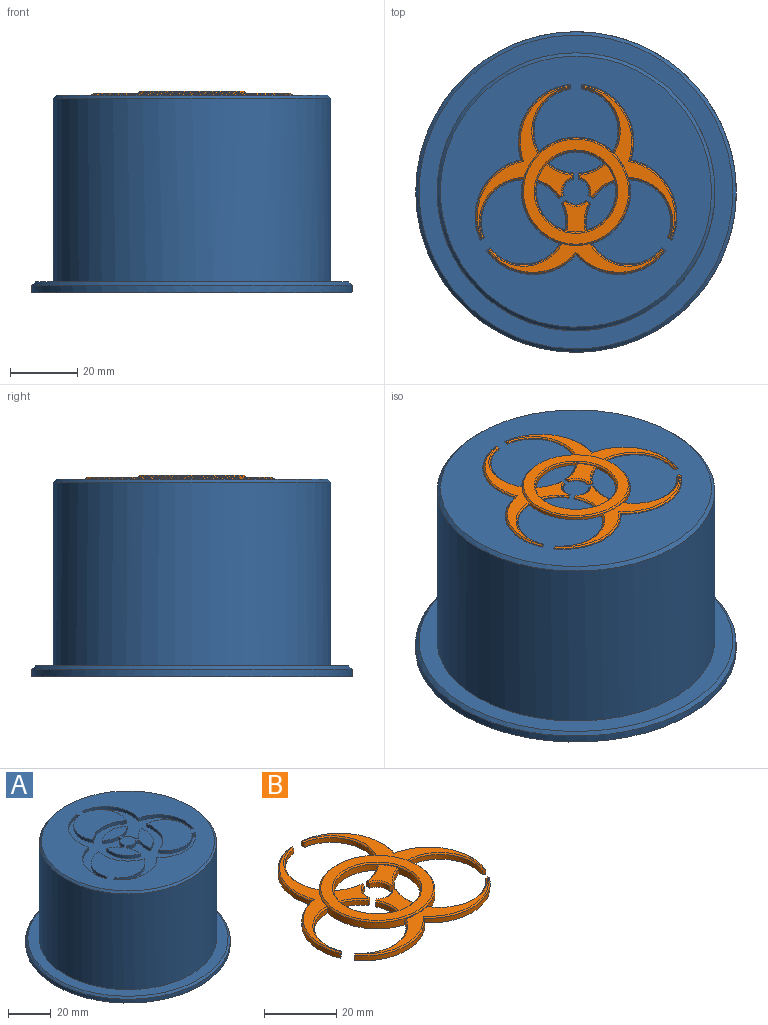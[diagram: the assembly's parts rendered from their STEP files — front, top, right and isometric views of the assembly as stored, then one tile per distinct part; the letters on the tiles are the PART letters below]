
ASSEMBLY  parts=2 mates=1
PART A: 85 faces, bbox 95.3x95.3x58.8 mm
  f0: plane 80.55x80.55mm, normal (0,0,1), area 3682.3mm2, adj f43,f46,f47,f48,f49,f53,f54,f55
  f1: plane 38.88x4.14mm, normal (0,0.71,-0.71), area 206.1mm2, adj f4,f12,f15,f35
  f2: plane 9.69x1.97mm, normal (0,1,-0.09), area 9.4mm2, adj f4,f15,f31
  f3: plane 38.88x4.14mm, normal (0,-0.71,-0.71), area 206.1mm2, adj f14,f15,f21,f39
  f4: cylinder r=50mm len=31.49mm, axis (1,0,0), area 469.7mm2, adj f1,f2,f15,f30
  f5: cylinder r=50mm len=34.5mm, axis (-0.5,-0.87,0), area 469.7mm2, adj f6,f7,f15,f41
  f6: plane 35.55x19.44mm, normal (0.61,-0.35,-0.71), area 206.1mm2, adj f5,f15,f24,f37
  f7: plane 9.69x1.72mm, normal (0.86,-0.5,-0.09), area 9.4mm2, adj f5,f15,f36
  f8: plane 35.55x19.44mm, normal (-0.61,0.35,-0.71), area 206.1mm2, adj f15,f27,f29,f34
  f9: plane 9.69x1.72mm, normal (-0.86,0.5,-0.09), area 9.4mm2, adj f15,f29,f33
  f10: plane 9.69x1.97mm, normal (0,-1,-0.09), area 9.4mm2, adj f15,f22,f25
  f11: plane 9.69x1.97mm, normal (0,1,-0.09), area 9.4mm2, adj f13,f15,f26
  f12: plane 38.88x4.14mm, normal (0,-0.71,-0.71), area 206.1mm2, adj f1,f15,f22,f24
  f13: cylinder r=50mm len=31.49mm, axis (1,0,0), area 469.7mm2, adj f11,f15,f21,f28
  f14: cylinder r=50mm len=31.49mm, axis (1,0,0), area 469.7mm2, adj f3,f15,f20,f40
  f15: cylinder r=38.88mm len=77.75mm, axis (0,0,-1), area 10153.5mm2, adj f1,f2,f3,f4,f5,f6,f7,f8
  f16: plane 95.25x95.25mm, normal (0,0,-1), area 2377.8mm2, adj f15,f17
  f17: cylinder r=47.62mm len=95.25mm, axis (0,0,-1), area 650.8mm2, adj f16,f42
  f18: plane 93.25x93.25mm, normal (0,0,1), area 1477.4mm2, adj f19,f42
  f19: cylinder r=41.27mm len=82.55mm, axis (0,0,-1), area 14146.9mm2, adj f18,f43
  f20: plane 9.69x1.97mm, normal (0,-1,-0.09), area 9.4mm2, adj f14,f15,f38
  f21: plane 38.88x4.14mm, normal (0,0.71,-0.71), area 206.1mm2, adj f3,f13,f15,f27
  f22: cylinder r=50mm len=31.49mm, axis (1,0,0), area 469.7mm2, adj f10,f12,f15,f23
  f23: cylinder r=50mm len=34.5mm, axis (-0.5,-0.87,0), area 469.7mm2, adj f15,f22,f24,f25
  f24: plane 33.67x22.92mm, normal (-0.61,0.35,-0.71), area 206.1mm2, adj f6,f12,f15,f23
  f25: plane 9.69x1.71mm, normal (-0.86,0.5,-0.09), area 9.4mm2, adj f10,f15,f23
  f26: plane 9.69x1.71mm, normal (0.86,-0.5,-0.09), area 9.4mm2, adj f11,f15,f28
  f27: plane 33.67x22.92mm, normal (0.61,-0.35,-0.71), area 206.1mm2, adj f8,f15,f21,f28
  f28: cylinder r=50mm len=34.5mm, axis (-0.5,-0.87,0), area 469.7mm2, adj f13,f15,f26,f27
  f29: cylinder r=50mm len=34.5mm, axis (-0.5,-0.87,0), area 469.7mm2, adj f8,f9,f15,f32
  f30: cylinder r=50mm len=34.5mm, axis (-0.5,0.87,0), area 469.7mm2, adj f4,f15,f31,f35
  f31: plane 9.69x1.71mm, normal (-0.86,-0.5,-0.09), area 9.4mm2, adj f2,f15,f30
  f32: cylinder r=50mm len=34.5mm, axis (-0.5,0.87,0), area 469.7mm2, adj f15,f29,f33,f34
  f33: plane 9.69x1.72mm, normal (0.86,0.5,-0.09), area 9.4mm2, adj f9,f15,f32
  f34: plane 35.55x19.44mm, normal (0.61,0.35,-0.71), area 206.1mm2, adj f8,f15,f32,f35
  f35: plane 33.67x22.92mm, normal (-0.61,-0.35,-0.71), area 206.1mm2, adj f1,f15,f30,f34
  f36: plane 9.69x1.72mm, normal (-0.86,-0.5,-0.09), area 9.4mm2, adj f7,f15,f41
  f37: plane 35.55x19.44mm, normal (-0.61,-0.35,-0.71), area 206.1mm2, adj f6,f15,f39,f41
  f38: plane 9.69x1.71mm, normal (0.86,0.5,-0.09), area 9.4mm2, adj f15,f20,f40
  f39: plane 33.67x22.92mm, normal (0.61,0.35,-0.71), area 206.1mm2, adj f3,f15,f37,f40
  f40: cylinder r=50mm len=34.5mm, axis (-0.5,0.87,0), area 469.7mm2, adj f14,f15,f38,f39
  f41: cylinder r=50mm len=34.5mm, axis (-0.5,0.87,0), area 469.7mm2, adj f5,f15,f36,f37
  f42: cone r=47.62mm half-angle=45deg, axis (0,0,-1), area 418.7mm2, adj f17,f18
  f43: cone r=41.27mm half-angle=45deg, axis (0,0,-1), area 362.3mm2, adj f0,f19
  f44: cylinder r=11.75mm len=14.06mm, axis (0,0,-1), area 31.4mm2, adj f59,f71,f77,f84
  f45: cylinder r=11.75mm len=16.24mm, axis (0,0,-1), area 31.4mm2, adj f57,f59,f66,f84
  f46: cylinder r=16.25mm len=18.99mm, axis (0,0,-1), area 42.1mm2, adj f0,f59,f63,f73
  f47: cylinder r=16.25mm len=21.93mm, axis (0,0,-1), area 42.1mm2, adj f0,f49,f59,f62
  f48: cylinder r=12.5mm len=17.17mm, axis (0,0,-1), area 42.3mm2, adj f0,f53,f59,f61
  f49: cylinder r=12.5mm len=18.38mm, axis (0,0,-1), area 42.3mm2, adj f0,f47,f56,f59
  f50: cylinder r=3.75mm len=4.86mm, axis (0,0,-1), area 11.1mm2, adj f51,f58,f59,f84
  f51: plane 1.75x1.6mm, normal (0.5,0.87,0), area 3.2mm2, adj f50,f52,f59,f84
  f52: cylinder r=12.5mm len=6.26mm, axis (0,0,-1), area 14.1mm2, adj f51,f59,f60,f84
  f53: plane 1.75x1.33mm, normal (0.5,0.87,0), area 2.7mm2, adj f0,f48,f54,f59
  f54: cylinder r=17.25mm len=23.92mm, axis (0,0,-1), area 53.7mm2, adj f0,f53,f55,f59
  f55: cylinder r=17.25mm len=22.43mm, axis (0,0,-1), area 53.7mm2, adj f0,f54,f56,f59
  f56: plane 1.75x1.53mm, normal (1,0,0), area 2.7mm2, adj f0,f49,f55,f59
  f57: cylinder r=12.5mm len=7.37mm, axis (0,0,-1), area 14.1mm2, adj f45,f58,f59,f84
  f58: plane 1.85x1.75mm, normal (1,0,0), area 3.2mm2, adj f50,f57,f59,f84
  f59: plane 60.05x56.54mm, normal (0,0,1), area 1152.5mm2, adj f44,f45,f46,f47,f48,f49,f50,f51
  f60: cylinder r=11.75mm len=14.06mm, axis (0,0,-1), area 31.4mm2, adj f52,f59,f82,f84
  f61: cylinder r=16.25mm len=18.99mm, axis (0,0,-1), area 42.1mm2, adj f0,f48,f59,f74
  f62: cylinder r=12.5mm len=18.38mm, axis (0,0,-1), area 42.3mm2, adj f0,f47,f59,f67
  f63: cylinder r=12.5mm len=17.17mm, axis (0,0,-1), area 42.3mm2, adj f0,f46,f59,f70
  f64: cylinder r=3.75mm len=4.86mm, axis (0,0,-1), area 11.1mm2, adj f59,f65,f72,f84
  f65: plane 1.85x1.75mm, normal (-1,0,0), area 3.2mm2, adj f59,f64,f66,f84
  f66: cylinder r=12.5mm len=7.37mm, axis (0,0,-1), area 14.1mm2, adj f45,f59,f65,f84
  f67: plane 1.75x1.53mm, normal (-1,0,0), area 2.7mm2, adj f0,f59,f62,f68
  f68: cylinder r=17.25mm len=22.43mm, axis (0,0,-1), area 53.7mm2, adj f0,f59,f67,f69
  f69: cylinder r=17.25mm len=23.92mm, axis (0,0,-1), area 53.7mm2, adj f0,f59,f68,f70
  f70: plane 1.75x1.33mm, normal (-0.5,0.87,0), area 2.7mm2, adj f0,f59,f63,f69
  f71: cylinder r=12.5mm len=6.26mm, axis (0,0,-1), area 14.1mm2, adj f44,f59,f72,f84
  f72: plane 1.75x1.6mm, normal (-0.5,0.87,0), area 3.2mm2, adj f59,f64,f71,f84
  f73: cylinder r=12.5mm len=20.53mm, axis (0,0,-1), area 42.3mm2, adj f0,f46,f59,f78
  f74: cylinder r=12.5mm len=20.53mm, axis (0,0,-1), area 42.3mm2, adj f0,f59,f61,f81
  f75: cylinder r=3.75mm len=5.61mm, axis (0,0,-1), area 11.1mm2, adj f59,f76,f83,f84
  f76: plane 1.75x1.6mm, normal (0.5,-0.87,0), area 3.2mm2, adj f59,f75,f77,f84
  f77: cylinder r=12.5mm len=7.87mm, axis (0,0,-1), area 14.1mm2, adj f44,f59,f76,f84
  f78: plane 1.75x1.33mm, normal (0.5,-0.87,0), area 2.7mm2, adj f0,f59,f73,f79
  f79: cylinder r=17.25mm len=26.76mm, axis (0,0,-1), area 53.7mm2, adj f0,f59,f78,f80
  f80: cylinder r=17.25mm len=26.76mm, axis (0,0,-1), area 53.7mm2, adj f0,f59,f79,f81
  f81: plane 1.75x1.33mm, normal (-0.5,-0.87,0), area 2.7mm2, adj f0,f59,f74,f80
  f82: cylinder r=12.5mm len=7.87mm, axis (0,0,-1), area 14.1mm2, adj f59,f60,f83,f84
  f83: plane 1.75x1.6mm, normal (-0.5,-0.87,0), area 3.2mm2, adj f59,f75,f82,f84
  f84: plane 23.5x23.03mm, normal (0,0,1), area 261.1mm2, adj f44,f45,f50,f51,f52,f57,f58,f60
PART B: 66 faces, bbox 59.6x56x2.6 mm
  f0: cylinder r=12.75mm len=17.31mm, axis (0,0,-1), area 39.6mm2, adj f6,f13,f15,f45
  f1: cylinder r=12.75mm len=19mm, axis (0,0,-1), area 39.6mm2, adj f9,f13,f15,f44
  f2: plane 10.48x9.77mm, normal (0,0,1), area 43.2mm2, adj f4,f11,f14,f51,f52,f53
  f3: cylinder r=4mm len=4.94mm, axis (0,0,-1), area 10.2mm2, adj f4,f11,f13,f53
  f4: plane 2x1.23mm, normal (-0.5,-0.87,0), area 2.7mm2, adj f2,f3,f5,f13,f51,f53
  f5: cylinder r=12.75mm len=6.51mm, axis (0,0,-1), area 13.3mm2, adj f4,f13,f14,f51
  f6: plane 2x0.9mm, normal (-0.5,-0.87,0), area 1.9mm2, adj f0,f7,f12,f13,f45,f58
  f7: cylinder r=17mm len=23.38mm, axis (0,0,-1), area 48.4mm2, adj f6,f8,f13,f58
  f8: cylinder r=17mm len=22.34mm, axis (0,0,-1), area 48.4mm2, adj f7,f9,f13,f59
  f9: plane 2x1.04mm, normal (-1,0,0), area 1.9mm2, adj f1,f8,f12,f13,f44,f59
  f10: cylinder r=12.75mm len=7.49mm, axis (0,0,-1), area 13.3mm2, adj f11,f13,f14,f52
  f11: plane 2x1.42mm, normal (-1,0,0), area 2.7mm2, adj f2,f3,f10,f13,f52,f53
  f12: plane 45.11x27.37mm, normal (0,0,1), area 124.7mm2, adj f6,f9,f15,f44,f45,f58,f59
  f13: plane 59.55x56.01mm, normal (0,0,-1), area 1016.8mm2, adj f0,f1,f3,f4,f5,f6,f7,f8
  f14: cylinder r=12mm len=24mm, axis (0,0,-1), area 128.7mm2, adj f2,f5,f10,f13,f18,f21,f26,f31
  f15: cylinder r=16mm len=32mm, axis (0,0,-1), area 166.6mm2, adj f0,f1,f12,f13,f16,f17,f28,f29
  f16: cylinder r=12.75mm len=19mm, axis (0,0,-1), area 39.6mm2, adj f13,f15,f22,f43
  f17: cylinder r=12.75mm len=17.31mm, axis (0,0,-1), area 39.6mm2, adj f13,f15,f25,f48
  f18: plane 10.48x9.77mm, normal (0,0,1), area 43.2mm2, adj f14,f20,f27,f55,f56,f57
  f19: cylinder r=4mm len=4.94mm, axis (0,0,-1), area 10.2mm2, adj f13,f20,f27,f55
  f20: plane 2x1.42mm, normal (1,0,0), area 2.7mm2, adj f13,f18,f19,f21,f55,f56
  f21: cylinder r=12.75mm len=7.49mm, axis (0,0,-1), area 13.3mm2, adj f13,f14,f20,f56
  f22: plane 2x1.04mm, normal (1,0,0), area 1.9mm2, adj f13,f16,f23,f28,f43,f63
  f23: cylinder r=17mm len=22.34mm, axis (0,0,-1), area 48.4mm2, adj f13,f22,f24,f63
  f24: cylinder r=17mm len=23.38mm, axis (0,0,-1), area 48.4mm2, adj f13,f23,f25,f62
  f25: plane 2x0.9mm, normal (0.5,-0.87,0), area 1.9mm2, adj f13,f17,f24,f28,f48,f62
  f26: cylinder r=12.75mm len=6.51mm, axis (0,0,-1), area 13.3mm2, adj f13,f14,f27,f57
  f27: plane 2x1.23mm, normal (0.5,-0.87,0), area 2.7mm2, adj f13,f18,f19,f26,f55,f57
  f28: plane 45.11x27.37mm, normal (0,0,1), area 124.7mm2, adj f15,f22,f25,f43,f48,f62,f63
  f29: cylinder r=12.75mm len=20.96mm, axis (0,0,-1), area 39.6mm2, adj f13,f15,f35,f47
  f30: cylinder r=12.75mm len=20.96mm, axis (0,0,-1), area 39.6mm2, adj f13,f15,f38,f46
  f31: plane 8.99x7.47mm, normal (0,0,1), area 43.2mm2, adj f14,f33,f40,f49,f50,f54
  f32: cylinder r=4mm len=5.71mm, axis (0,0,-1), area 10.2mm2, adj f13,f33,f40,f54
  f33: plane 2x1.23mm, normal (-0.5,0.87,0), area 2.7mm2, adj f13,f31,f32,f34,f49,f54
  f34: cylinder r=12.75mm len=8.08mm, axis (0,0,-1), area 13.3mm2, adj f13,f14,f33,f49
  f35: plane 2x0.9mm, normal (-0.5,0.87,0), area 1.9mm2, adj f13,f29,f36,f41,f47,f60
  f36: cylinder r=17mm len=26.39mm, axis (0,0,-1), area 48.4mm2, adj f13,f35,f37,f60
  f37: cylinder r=17mm len=26.39mm, axis (0,0,-1), area 48.4mm2, adj f13,f36,f38,f61
  f38: plane 2x0.9mm, normal (0.5,0.87,0), area 1.9mm2, adj f13,f30,f37,f41,f46,f61
  f39: cylinder r=12.75mm len=8.08mm, axis (0,0,-1), area 13.3mm2, adj f13,f14,f40,f50
  f40: plane 2x1.23mm, normal (0.5,0.87,0), area 2.7mm2, adj f13,f31,f32,f39,f50,f54
  f41: plane 52.09x8.52mm, normal (0,0,1), area 124.7mm2, adj f15,f35,f38,f46,f47,f60,f61
  f42: plane 31.2x31.2mm, normal (0,0,1), area 281.5mm2, adj f64,f65
  f43: cone r=13.15mm half-angle=45deg, axis (0,0,1), area 14.3mm2, adj f15,f16,f22,f28
  f44: cone r=12.75mm half-angle=45deg, axis (0,0,1), area 14.3mm2, adj f1,f9,f12,f15
  f45: cone r=13.15mm half-angle=45deg, axis (0,0,1), area 14.3mm2, adj f0,f6,f12,f15
  f46: cone r=12.75mm half-angle=45deg, axis (0,0,1), area 14.3mm2, adj f15,f30,f38,f41
  f47: cone r=13.15mm half-angle=45deg, axis (0,0,1), area 14.3mm2, adj f15,f29,f35,f41
  f48: cone r=12.75mm half-angle=45deg, axis (0,0,1), area 14.3mm2, adj f15,f17,f25,f28
  f49: cone r=13.15mm half-angle=45deg, axis (0,0,1), area 4.8mm2, adj f14,f31,f33,f34
  f50: cone r=12.75mm half-angle=45deg, axis (0,0,1), area 4.8mm2, adj f14,f31,f39,f40
  f51: cone r=13.15mm half-angle=45deg, axis (0,0,1), area 4.8mm2, adj f2,f4,f5,f14
  f52: cone r=12.75mm half-angle=45deg, axis (0,0,1), area 4.8mm2, adj f2,f10,f11,f14
  f53: cone r=4mm half-angle=45deg, axis (0,0,1), area 3.8mm2, adj f2,f3,f4,f11
  f54: cone r=4mm half-angle=45deg, axis (0,0,1), area 3.8mm2, adj f31,f32,f33,f40
  f55: cone r=4mm half-angle=45deg, axis (0,0,1), area 3.8mm2, adj f18,f19,f20,f27
  f56: cone r=13.15mm half-angle=45deg, axis (0,0,1), area 4.8mm2, adj f14,f18,f20,f21
  f57: cone r=12.75mm half-angle=45deg, axis (0,0,1), area 4.8mm2, adj f14,f18,f26,f27
  f58: cone r=17mm half-angle=45deg, axis (0,0,-1), area 17mm2, adj f6,f7,f12,f59
  f59: cone r=16.6mm half-angle=45deg, axis (0,0,-1), area 17mm2, adj f8,f9,f12,f58
  f60: cone r=17mm half-angle=45deg, axis (0,0,-1), area 17mm2, adj f35,f36,f41,f61
  f61: cone r=16.6mm half-angle=45deg, axis (0,0,-1), area 17mm2, adj f37,f38,f41,f60
  f62: cone r=16.6mm half-angle=45deg, axis (0,0,-1), area 17mm2, adj f24,f25,f28,f63
  f63: cone r=17mm half-angle=45deg, axis (0,0,-1), area 17mm2, adj f22,f23,f28,f62
  f64: cone r=15.6mm half-angle=45deg, axis (0,0,-1), area 56.2mm2, adj f15,f42
  f65: cone r=12mm half-angle=45deg, axis (0,0,1), area 43.4mm2, adj f14,f42
PLACE A at identity fixed
PLACE B t=(0,0,57.22)mm
MATE fastened A.f15 <-> B.f3  axis (0,0,1) through (0,0,58.72)mm
